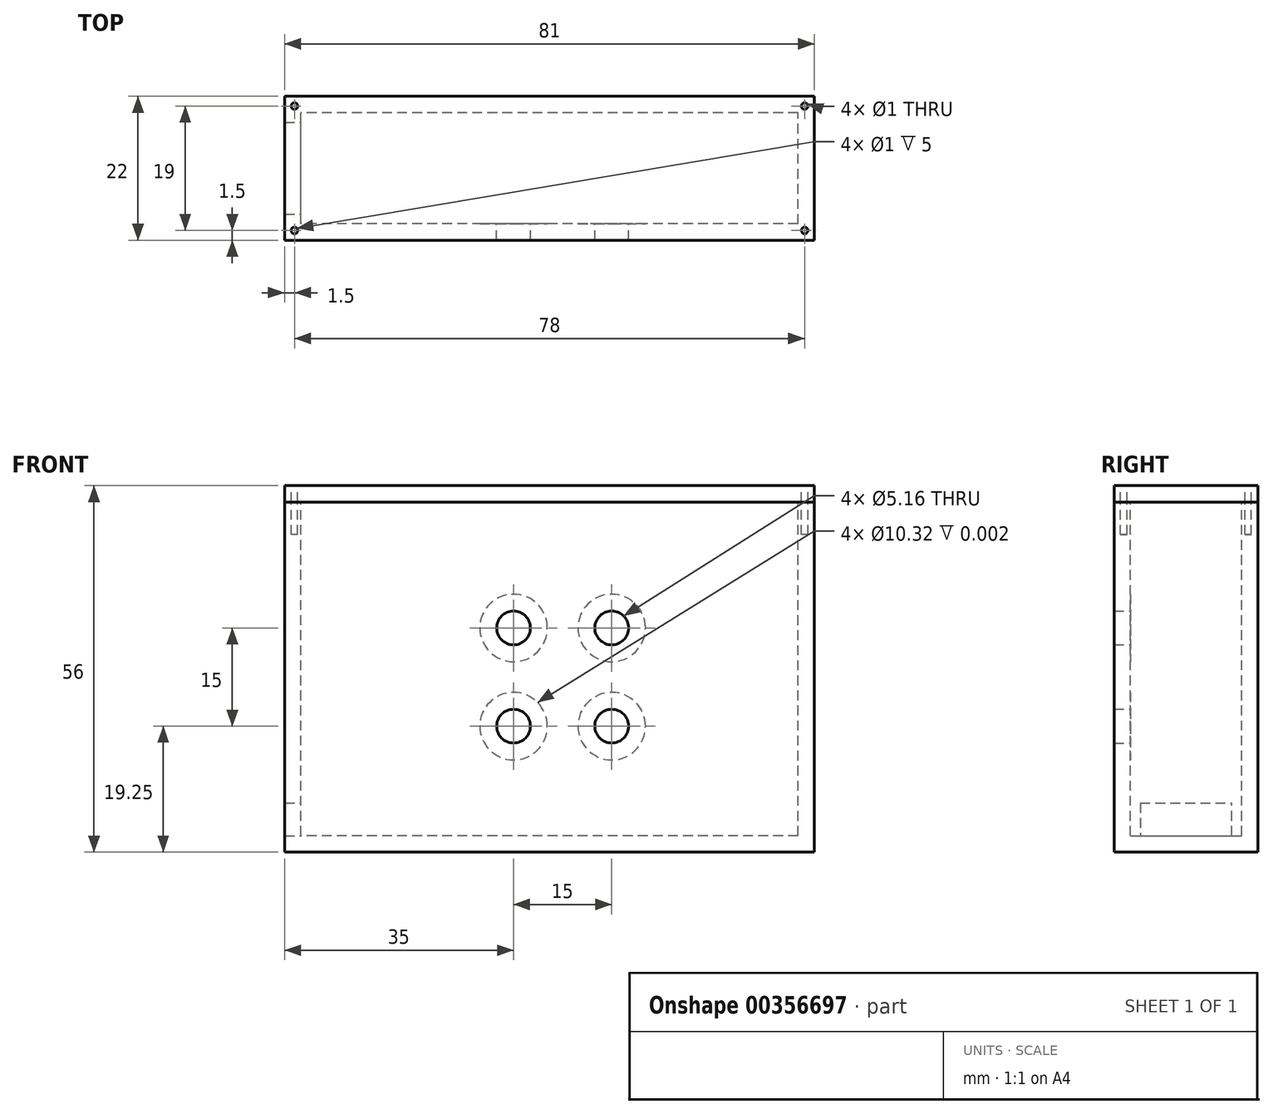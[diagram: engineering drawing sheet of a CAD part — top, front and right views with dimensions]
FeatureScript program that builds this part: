
annotation { "Feature Type Name" : "Feature", "Feature Type Description" : "" }
export const myFeature = defineFeature(function(context is Context, id is Id, definition is map)
    precondition{}
    {
        {
            var Q0;
            Q0=qCreatedBy(makeId("Front.planeOp"),FACE);
            var sketch = newSketch(context, id + "F0", { "sketchPlane" : qUnion([Q0])});
            skLineSegment(sketch, "E0.bottom", {"start": v(40.5, -26.75) * mm, "end": v(-40.5, -26.75) * mm});
            skLineSegment(sketch, "E0.top", {"start": v(40.5, 26.75) * mm, "end": v(-40.5, 26.75) * mm});
            skLineSegment(sketch, "E0.left", {"start": v(40.5, -26.75) * mm, "end": v(40.5, 26.75) * mm});
            skLineSegment(sketch, "E0.right", {"start": v(-40.5, -26.75) * mm, "end": v(-40.5, 26.75) * mm});
            skPoint(sketch, "E0.middle", {"position": v(0, 0) * mm});
            skSolve(sketch);
        }
        {
            var Q0;
            Q0=qSketchRegion(id+"F0",true);
            extrude(context, id + "F1", {"entities" : qUnion([Q0]), "endBound" : BoundingType.SYMMETRIC, "depth" : 22 * mm});
        }
        {
            var Q0;
            Q0=makeQuery(id+"F1.opExtrude","SWEPT_FACE",FACE,{"disambiguationData":[OSD([sQuery(id+"F0.wireOp",EDGE,"E0.top")])]});
            shell(context, id + "F2", {"entities" : qUnion([Q0]), "thickness" : 2.5 * mm});
        }
        {
            var Q0;
            Q0=qCreatedBy(makeId("Right.planeOp"),FACE);
            var sketch = newSketch(context, id + "F3", { "sketchPlane" : qUnion([Q0])});
            skLineSegment(sketch, "E1", {"start": v(7, -19.25) * mm, "end": v(7, -24.25) * mm});
            skLineSegment(sketch, "E2", {"start": v(7, -24.25) * mm, "end": v(-7, -24.25) * mm});
            skLineSegment(sketch, "E3", {"start": v(-7, -24.25) * mm, "end": v(-7, -19.25) * mm});
            skLineSegment(sketch, "E4", {"start": v(7, -19.25) * mm, "end": v(-7, -19.25) * mm});
            skSolve(sketch);
        }
        {
            var Q0;
            Q0=qSketchRegion(id+"F3",true);
            extrude(context, id + "F4", {"entities" : qUnion([Q0]), "operationType" : NewBodyOperationType.REMOVE, "oppositeDirection" : true, "depth" : 49.6 * mm});
        }
        {
            var Q0;
            Q0=qCreatedBy(makeId("Front.planeOp"),FACE);
            var sketch = newSketch(context, id + "F5", { "sketchPlane" : qUnion([Q0])});
            skCircle(sketch, "E5", {"center": v(-5.5, -7.5) * mm, "radius": 2.58 * mm});
            skPoint(sketch, "E5.first.point", {"position": v(-7.75, -6.25) * mm});
            skPoint(sketch, "E5.second.point", {"position": v(-4.13, -9.68) * mm});
            skPoint(sketch, "E5.third.point", {"position": v(-3.36, -6.06) * mm});
            skCircle(sketch, "E6", {"center": v(9.5, -7.5) * mm, "radius": 2.58 * mm});
            skCircle(sketch, "E7", {"center": v(9.5, 7.5) * mm, "radius": 2.58 * mm});
            skCircle(sketch, "E8", {"center": v(-5.5, 7.5) * mm, "radius": 2.58 * mm});
            skLineSegment(sketch, "E9", {"start": v(-5.5, 7.5) * mm, "end": v(-5.5, -7.5) * mm, "construction": true});
            skLineSegment(sketch, "E10", {"start": v(-5.5, -7.5) * mm, "end": v(9.5, -7.5) * mm, "construction": true});
            skLineSegment(sketch, "E11", {"start": v(9.5, -7.5) * mm, "end": v(9.5, 7.5) * mm, "construction": true});
            skLineSegment(sketch, "E12", {"start": v(9.5, 7.5) * mm, "end": v(-5.5, 7.5) * mm, "construction": true});
            skSolve(sketch);
        }
        {
            var Q0;
            Q0=qSketchRegion(id+"F5",true);
            extrude(context, id + "F6", {"entities" : qUnion([Q0]), "operationType" : NewBodyOperationType.REMOVE, "depth" : 25 * mm});
        }
        {
            var Q0;
            Q0=qCreatedBy(makeId("Top.planeOp"),FACE);
            cPlane(context, id + "F7", {"entities" : qUnion([Q0]), "cplaneType" : CPlaneType.OFFSET, "offset" : (53.5 / 2) * mm, "width" : 150 * mm, "height" : 150 * mm});
        }
        {
            var Q0;
            Q0=qCreatedBy(id+"F7.planeOp",FACE);
            var sketch = newSketch(context, id + "F8", { "sketchPlane" : qUnion([Q0])});
            skLineSegment(sketch, "E13.bottom", {"start": v(40.5, -11) * mm, "end": v(-40.5, -11) * mm});
            skLineSegment(sketch, "E13.top", {"start": v(40.5, 11) * mm, "end": v(-40.5, 11) * mm});
            skLineSegment(sketch, "E13.left", {"start": v(40.5, -11) * mm, "end": v(40.5, 11) * mm});
            skLineSegment(sketch, "E13.right", {"start": v(-40.5, -11) * mm, "end": v(-40.5, 11) * mm});
            skPoint(sketch, "E13.middle", {"position": v(0, 0) * mm});
            skSolve(sketch);
        }
        {
            var Q0;
            Q0=qSketchRegion(id+"F8",true);
            extrude(context, id + "F9", {"entities" : qUnion([Q0]), "depth" : 2.5 * mm});
        }
        {
            var Q0;
            Q0=qCreatedBy(id+"F7.planeOp",FACE);
            var sketch = newSketch(context, id + "F10", { "sketchPlane" : qUnion([Q0])});
            skCircle(sketch, "E14", {"center": v(-39, 9.5) * mm, "radius": 0.5 * mm});
            skCircle(sketch, "E15", {"center": v(-39, -9.5) * mm, "radius": 0.5 * mm});
            skCircle(sketch, "E16", {"center": v(39, -9.5) * mm, "radius": 0.5 * mm});
            skCircle(sketch, "E17", {"center": v(39, 9.5) * mm, "radius": 0.5 * mm});
            skSolve(sketch);
        }
        {
            var Q0;
            Q0=makeQuery(id+"F1.opExtrude","SWEPT_FACE",FACE,{"disambiguationData":[OSD([sQuery(id+"F0.wireOp",EDGE,"E0.top")])]});
            var sketch = newSketch(context, id + "F11", { "sketchPlane" : qUnion([Q0])});
            skCircle(sketch, "E18", {"center": v(-39, 9.5) * mm, "radius": 0.5 * mm});
            skPoint(sketch, "E18.first.point", {"position": v(-39.47, 9.66) * mm});
            skPoint(sketch, "E18.second.point", {"position": v(-38.5, 9.5) * mm});
            skPoint(sketch, "E18.third.point", {"position": v(-38.56, 9.73) * mm});
            skCircle(sketch, "E19", {"center": v(-39, -9.5) * mm, "radius": 0.5 * mm});
            skCircle(sketch, "E20", {"center": v(39, -9.5) * mm, "radius": 0.5 * mm});
            skCircle(sketch, "E21", {"center": v(39, 9.5) * mm, "radius": 0.5 * mm});
            skSolve(sketch);
        }
        {
            var Q0;
            Q0=qSketchRegion(id+"F11",true);
            extrude(context, id + "F12", {"entities" : qUnion([Q0]), "operationType" : NewBodyOperationType.REMOVE, "oppositeDirection" : true, "depth" : 5 * mm});
        }
        {
            var Q0;
            Q0=qSketchRegion(id+"F10",true);
            extrude(context, id + "F13", {"entities" : qUnion([Q0]), "operationType" : NewBodyOperationType.REMOVE, "endBound" : BoundingType.SYMMETRIC, "oppositeDirection" : true, "depth" : 10 * mm});
        }
        {
            var Q0;
            {var subQ0=sQuery(id+"F0.wireOp",EDGE,"E0.right");var subQ1=sQuery(id+"F0.wireOp",EDGE,"E0.left");var subQ2=sQuery(id+"F0.wireOp",EDGE,"E0.top");var subQ3=sQuery(id+"F0.wireOp",EDGE,"E0.bottom");Q0=makeQuery(id+"F2.opShell","OFFSET_FACE",FACE,{"disambiguationData":[OSD([subQ3,subQ2,subQ1,subQ0]),TDD([makeQuery(id+"F1.opExtrude","CAP_FACE",FACE,{"disambiguationData":[OSD([subQ3,subQ2,subQ1,subQ0])],"isStart":false})])]});}
            var sketch = newSketch(context, id + "F14", { "sketchPlane" : qUnion([Q0])});
            skCircle(sketch, "E22", {"center": v(5.5, -7.5) * mm, "radius": 5.16 * mm});
            skCircle(sketch, "E23", {"center": v(5.5, 7.5) * mm, "radius": 5.16 * mm});
            skCircle(sketch, "E24", {"center": v(-9.5, -7.5) * mm, "radius": 5.16 * mm});
            skCircle(sketch, "E25", {"center": v(-9.5, 7.5) * mm, "radius": 5.16 * mm});
            skSolve(sketch);
        }
        {
            var Q0;
            Q0=qSketchRegion(id+"F14",true);
            extrude(context, id + "F15", {"entities" : qUnion([Q0]), "operationType" : NewBodyOperationType.REMOVE, "oppositeDirection" : true, "depth" : 1 / 406.4 * mm});
        }
    });
